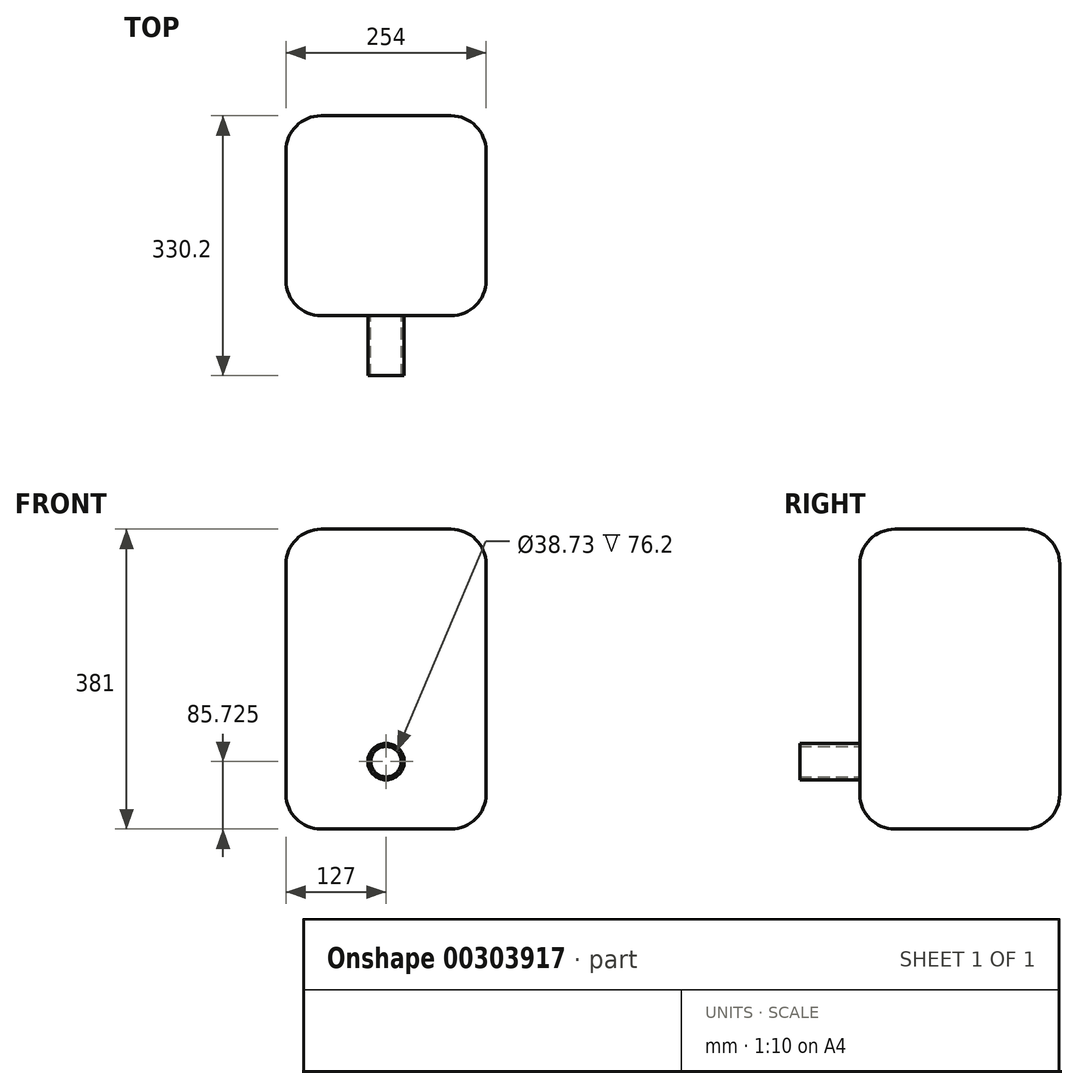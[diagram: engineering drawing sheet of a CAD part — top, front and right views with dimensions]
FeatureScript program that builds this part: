
annotation { "Feature Type Name" : "Feature", "Feature Type Description" : "" }
export const myFeature = defineFeature(function(context is Context, id is Id, definition is map)
    precondition{}
    {
        {
            var Q0;
            Q0=qCreatedBy(makeId("Front.planeOp"),FACE);
            var sketch = newSketch(context, id + "F0", { "sketchPlane" : qUnion([Q0])});
            skLineSegment(sketch, "E0", {"start": v(0, 0) * mm, "end": v(0, -127) * mm, "construction": true});
            skLineSegment(sketch, "E1", {"start": v(0, -127) * mm, "end": v(-127, -127) * mm});
            skLineSegment(sketch, "E2", {"start": v(-127, -127) * mm, "end": v(-127, 254) * mm});
            skLineSegment(sketch, "E3", {"start": v(-127, 254) * mm, "end": v(127, 254) * mm});
            skLineSegment(sketch, "E4", {"start": v(127, 254) * mm, "end": v(127, -127) * mm});
            skLineSegment(sketch, "E5", {"start": v(127, -127) * mm, "end": v(0, -127) * mm});
            skSolve(sketch);
        }
        {
            var Q0;
            Q0 = qSketchRegion(id + "F0", true);
            extrude(context, id + "F1", {"entities" : qUnion([Q0]), "endBound" : BoundingType.SYMMETRIC, "depth" : 254 * mm});
        }
        {
            var Q0;
            Q0=makeQuery(id+"F1.opExtrude","CAP_EDGE",EDGE,{"disambiguationData":[OSD([sQuery(id+"F0.wireOp",EDGE,"E3")])],"isStart":false});
            var Q1;
            Q1=makeQuery(id+"F1.opExtrude","SWEPT_EDGE",EDGE,{"disambiguationData":[OSD([sQuery(id+"F0.wireOp",EDGE,"E3"),sQuery(id+"F0.wireOp",EDGE,"E4")])]});
            var Q2;
            Q2=makeQuery(id+"F1.opExtrude","CAP_FACE",FACE,{"disambiguationData":[OSD([sQuery(id+"F0.wireOp",EDGE,"E1"),sQuery(id+"F0.wireOp",EDGE,"E2"),sQuery(id+"F0.wireOp",EDGE,"E3"),sQuery(id+"F0.wireOp",EDGE,"E4"),sQuery(id+"F0.wireOp",EDGE,"E5")])],"isStart":false});
            var Q3;
            Q3=makeQuery(id+"F1.opExtrude","SWEPT_EDGE",EDGE,{"disambiguationData":[OSD([sQuery(id+"F0.wireOp",EDGE,"E4"),sQuery(id+"F0.wireOp",EDGE,"E5")])]});
            var Q4;
            Q4=makeQuery(id+"F1.opExtrude","SWEPT_FACE",FACE,{"disambiguationData":[OSD([sQuery(id+"F0.wireOp",EDGE,"E3")])]});
            var Q5;
            Q5=makeQuery(id+"F1.opExtrude","SWEPT_FACE",FACE,{"disambiguationData":[OSD([sQuery(id+"F0.wireOp",EDGE,"E2")])]});
            var Q6;
            Q6=makeQuery(id+"F1.opExtrude","CAP_EDGE",EDGE,{"disambiguationData":[OSD([sQuery(id+"F0.wireOp",EDGE,"E1"),sQuery(id+"F0.wireOp",EDGE,"E5")])],"isStart":true});
            var Q7;
            Q7=makeQuery(id+"F1.opExtrude","CAP_EDGE",EDGE,{"disambiguationData":[OSD([sQuery(id+"F0.wireOp",EDGE,"E4")])],"isStart":true});
            fillet(context, id + "F2", {"entities" : qUnion([Q0, Q1, Q2, Q3, Q4, Q5, Q6, Q7]), "radius" : 44.45 * mm, "tangentPropagation" : true, "allowEdgeOverflow" : false});
        }
        {
            var Q0;
            Q0=makeQuery(id+"F1.opExtrude","CAP_FACE",FACE,{"disambiguationData":[OSD([sQuery(id+"F0.wireOp",EDGE,"E1"),sQuery(id+"F0.wireOp",EDGE,"E2"),sQuery(id+"F0.wireOp",EDGE,"E3"),sQuery(id+"F0.wireOp",EDGE,"E4"),sQuery(id+"F0.wireOp",EDGE,"E5")])],"isStart":false});
            var sketch = newSketch(context, id + "F3", { "sketchPlane" : qUnion([Q0])});
            skLineSegment(sketch, "E6", {"start": v(0, 0) * mm, "end": v(0, -82.55) * mm, "construction": true});
            skCircle(sketch, "E7", {"center": v(0, -41.27) * mm, "radius": 23.05 * mm});
            skCircle(sketch, "E8", {"center": v(0, -41.27) * mm, "radius": 19.37 * mm});
            skSolve(sketch);
        }
        {
            var Q0;
            Q0=makeQuery(id+"F3.imprint","IMPRINT",FACE,{"disambiguationData":[TD([[makeQuery(id+"F3.imprint","IMPRINT",EDGE,{"derivedFrom":sQuery(id+"F3.wireOp",EDGE,"E7")}),1.0]])]});
            extrude(context, id + "F4", {"entities" : qUnion([Q0]), "operationType" : NewBodyOperationType.ADD, "depth" : 76.2 * mm});
        }
    });
